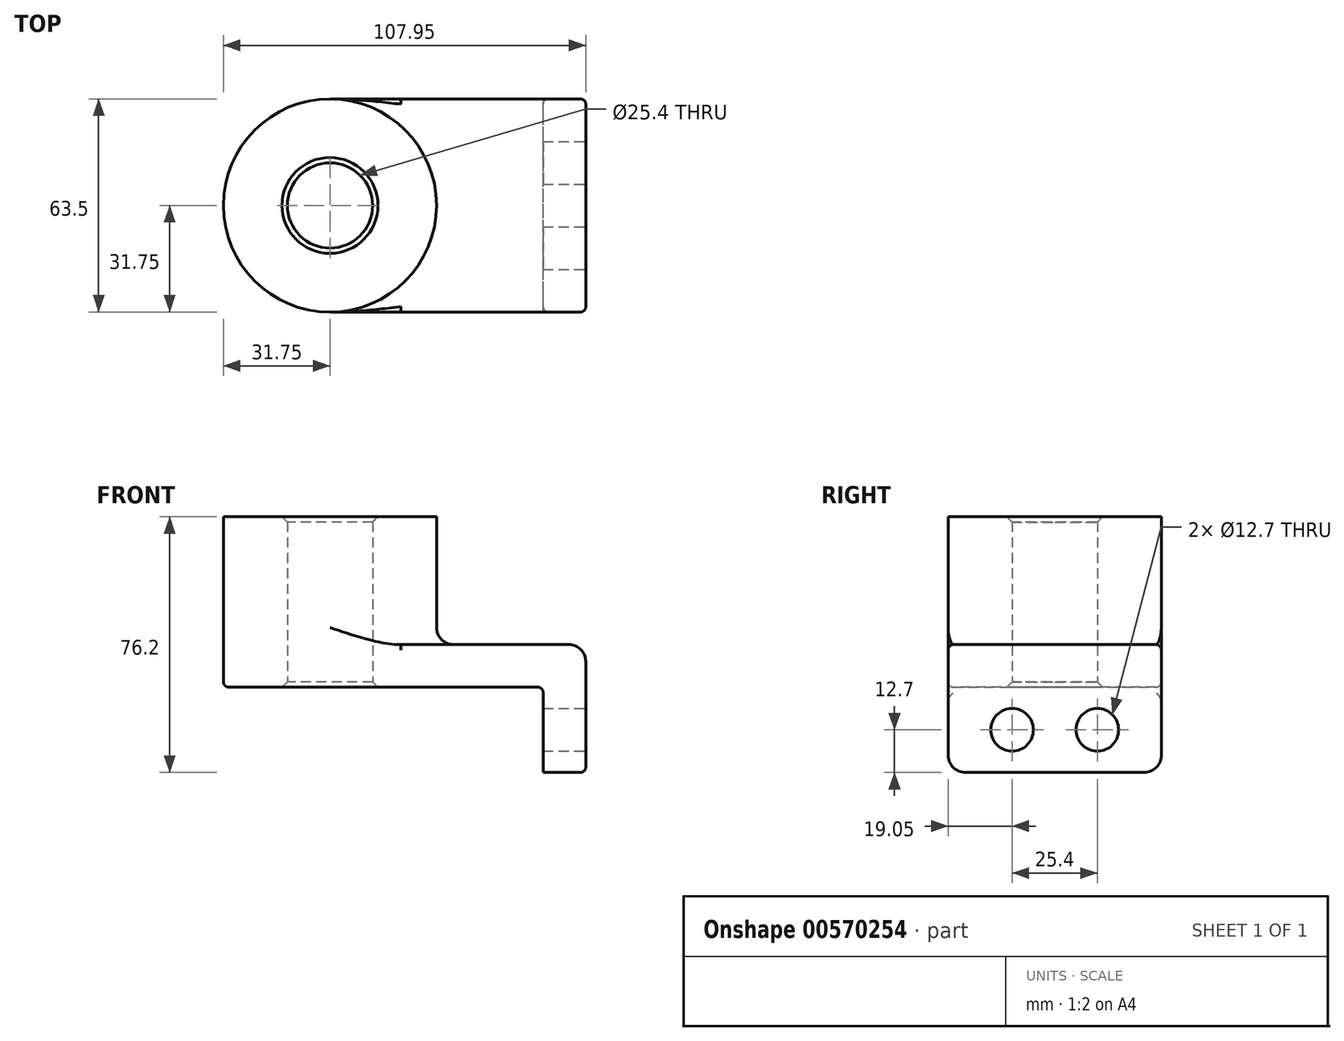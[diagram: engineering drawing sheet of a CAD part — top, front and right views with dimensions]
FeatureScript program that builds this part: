
annotation { "Feature Type Name" : "Feature", "Feature Type Description" : "" }
export const myFeature = defineFeature(function(context is Context, id is Id, definition is map)
    precondition{}
    {
        {
            var Q0;
            Q0=qCreatedBy(makeId("Top.planeOp"),FACE);
            var sketch = newSketch(context, id + "F0", { "sketchPlane" : qUnion([Q0])});
            skLineSegment(sketch, "E0.bottom", {"start": v(-38.1, 31.75) * mm, "end": v(38.1, 31.75) * mm});
            skLineSegment(sketch, "E0.top", {"start": v(-38.1, -31.75) * mm, "end": v(38.1, -31.75) * mm});
            skLineSegment(sketch, "E0.left", {"start": v(-38.1, 31.75) * mm, "end": v(-38.1, -31.75) * mm});
            skLineSegment(sketch, "E0.right", {"start": v(38.1, 31.75) * mm, "end": v(38.1, -31.75) * mm});
            skPoint(sketch, "E0.middle", {"position": v(0, 0) * mm});
            skCircle(sketch, "E1", {"center": v(-38.1, 0) * mm, "radius": 31.75 * mm});
            skCircle(sketch, "E2", {"center": v(-38.1, 0) * mm, "radius": 12.7 * mm});
            skSolve(sketch);
        }
        {
            var Q0;
            Q0 = qSketchRegion(id + "F0", true);
            extrude(context, id + "F1", {"entities" : qUnion([Q0]), "depth" : 12.7 * mm, "offsetDistance" : 25.4 * mm});
        }
        {
            var Q0;
            {var subQ1=sQuery(id+"F0.wireOp",EDGE,"E0.left");var subQ3=sQuery(id+"F0.wireOp",EDGE,"E2");var subQ4=makeQuery(id+"F0.imprint","INTERSECT",VERTEX,{"disambiguationData":[OD(0.0)],"derivedFrom":[subQ1,subQ3]});Q0=makeQuery(id+"F0.imprint","IMPRINT",FACE,{"disambiguationData":[TD([[makeQuery(id+"F0.imprint","IMPRINT",EDGE,{"disambiguationData":[TD([[subQ4,-1.0]])],"derivedFrom":subQ3}),-1.0]])]});}
            var Q1;
            {var subQ1=sQuery(id+"F0.wireOp",EDGE,"E0.left");var subQ3=sQuery(id+"F0.wireOp",EDGE,"E2");var subQ4=makeQuery(id+"F0.imprint","INTERSECT",VERTEX,{"disambiguationData":[OD(0.0)],"derivedFrom":[subQ1,subQ3]});Q1=makeQuery(id+"F0.imprint","IMPRINT",FACE,{"disambiguationData":[TD([[makeQuery(id+"F0.imprint","IMPRINT",EDGE,{"disambiguationData":[TD([[subQ4,1.0]])],"derivedFrom":subQ3}),-1.0]])]});}
            extrude(context, id + "F2", {"entities" : qUnion([Q0, Q1]), "operationType" : NewBodyOperationType.ADD, "depth" : 50.8 * mm, "offsetDistance" : 25.4 * mm});
        }
        {
            var Q0;
            Q0=makeQuery(id+"F1.opExtrude","SWEPT_FACE",FACE,{"disambiguationData":[OSD([sQuery(id+"F0.wireOp",EDGE,"E0.right")])]});
            var sketch = newSketch(context, id + "F3", { "sketchPlane" : qUnion([Q0])});
            skLineSegment(sketch, "E3.bottom", {"start": v(-31.75, 12.7) * mm, "end": v(31.75, 12.7) * mm});
            skLineSegment(sketch, "E3.top", {"start": v(-31.75, -25.4) * mm, "end": v(31.75, -25.4) * mm});
            skLineSegment(sketch, "E3.left", {"start": v(-31.75, 12.7) * mm, "end": v(-31.75, -25.4) * mm});
            skLineSegment(sketch, "E3.right", {"start": v(31.75, 12.7) * mm, "end": v(31.75, -25.4) * mm});
            skCircle(sketch, "E4", {"center": v(-12.7, -12.7) * mm, "radius": 6.35 * mm});
            skLineSegment(sketch, "E5", {"start": v(0, 0) * mm, "end": v(0, -25.4) * mm, "construction": true});
            skCircle(sketch, "E6.MirrorC", {"center": v(12.7, -12.7) * mm, "radius": 6.35 * mm});
            skSolve(sketch);
        }
        {
            var Q0;
            Q0 = qSketchRegion(id + "F3", true);
            extrude(context, id + "F4", {"entities" : qUnion([Q0]), "operationType" : NewBodyOperationType.ADD, "oppositeDirection" : true, "depth" : 12.7 * mm, "offsetDistance" : 25.4 * mm});
        }
        {
            var Q0;
            {var subQ0=sQuery(id+"F0.wireOp",EDGE,"E1");Q0=makeQuery(id+"F2.boolean.opBoolean","INTERSECT",EDGE,{"derivedFrom":[makeQuery(id+"F1.opExtrude","CAP_FACE",FACE,{"disambiguationData":[OSD([sQuery(id+"F0.wireOp",EDGE,"E0.bottom"),sQuery(id+"F0.wireOp",EDGE,"E0.top"),sQuery(id+"F0.wireOp",EDGE,"E0.right"),subQ0,sQuery(id+"F0.wireOp",EDGE,"E2")])],"isStart":false}),makeQuery(id+"F2.opExtrude","SWEPT_FACE",FACE,{"disambiguationData":[OSD([subQ0])]})]});}
            var Q1;
            Q1=makeQuery(id+"F1.opExtrude","CAP_EDGE",EDGE,{"disambiguationData":[OSD([sQuery(id+"F0.wireOp",EDGE,"E0.right")])],"isStart":false});
            var Q2;
            Q2=makeQuery(id+"F4.opExtrude","SWEPT_EDGE",EDGE,{"disambiguationData":[OSD([sQuery(id+"F3.wireOp",EDGE,"E3.top"),sQuery(id+"F3.wireOp",EDGE,"E3.left")])]});
            var Q3;
            Q3=makeQuery(id+"F4.opExtrude","SWEPT_EDGE",EDGE,{"disambiguationData":[OSD([sQuery(id+"F3.wireOp",EDGE,"E3.top"),sQuery(id+"F3.wireOp",EDGE,"E3.right")])]});
            fillet(context, id + "F5", {"entities" : qUnion([Q0, Q1, Q2, Q3]), "radius" : 5.08 * mm, "tangentPropagation" : true, "allowEdgeOverflow" : false});
        }
        {
            var Q0;
            Q0=makeQuery(id+"F1.opExtrude","CAP_EDGE",EDGE,{"disambiguationData":[OSD([sQuery(id+"F0.wireOp",EDGE,"E0.top")])],"isStart":false});
            var Q1;
            Q1=makeQuery(id+"F1.opExtrude","CAP_EDGE",EDGE,{"disambiguationData":[OSD([sQuery(id+"F0.wireOp",EDGE,"E0.top")])],"isStart":true});
            var Q2;
            Q2=makeQuery(id+"F4.boolean.opBoolean","INTERSECT",EDGE,{"derivedFrom":[makeQuery(id+"F1.opExtrude","CAP_FACE",FACE,{"disambiguationData":[OSD([sQuery(id+"F0.wireOp",EDGE,"E0.bottom"),sQuery(id+"F0.wireOp",EDGE,"E0.top"),sQuery(id+"F0.wireOp",EDGE,"E0.right"),sQuery(id+"F0.wireOp",EDGE,"E1"),sQuery(id+"F0.wireOp",EDGE,"E2")])],"isStart":true}),makeQuery(id+"F4.opExtrude","CAP_FACE",FACE,{"disambiguationData":[OSD([sQuery(id+"F3.wireOp",EDGE,"E3.bottom"),sQuery(id+"F3.wireOp",EDGE,"E3.top"),sQuery(id+"F3.wireOp",EDGE,"E3.left"),sQuery(id+"F3.wireOp",EDGE,"E3.right"),sQuery(id+"F3.wireOp",EDGE,"E4"),sQuery(id+"F3.wireOp",EDGE,"E6.MirrorC")])],"isStart":false})]});
            fillet(context, id + "F6", {"entities" : qUnion([Q0, Q1, Q2]), "radius" : 1.59 * mm, "tangentPropagation" : true, "allowEdgeOverflow" : false});
        }
        {
            var Q0;
            {var subQ0=sQuery(id+"F0.wireOp",EDGE,"E2");Q0=makeQuery(id+"F2.boolean.opBoolean","MERGE",FACE,{"derivedFrom":[makeQuery(id+"F1.opExtrude","SWEPT_FACE",FACE,{"disambiguationData":[OSD([subQ0])]}),makeQuery(id+"F2.opExtrude","SWEPT_FACE",FACE,{"disambiguationData":[OSD([subQ0])]})]});}
            chamfer(context, id + "F7", {"entities" : qUnion([Q0]), "width" : 1.59 * mm, "tangentPropagation" : true});
        }
    });
